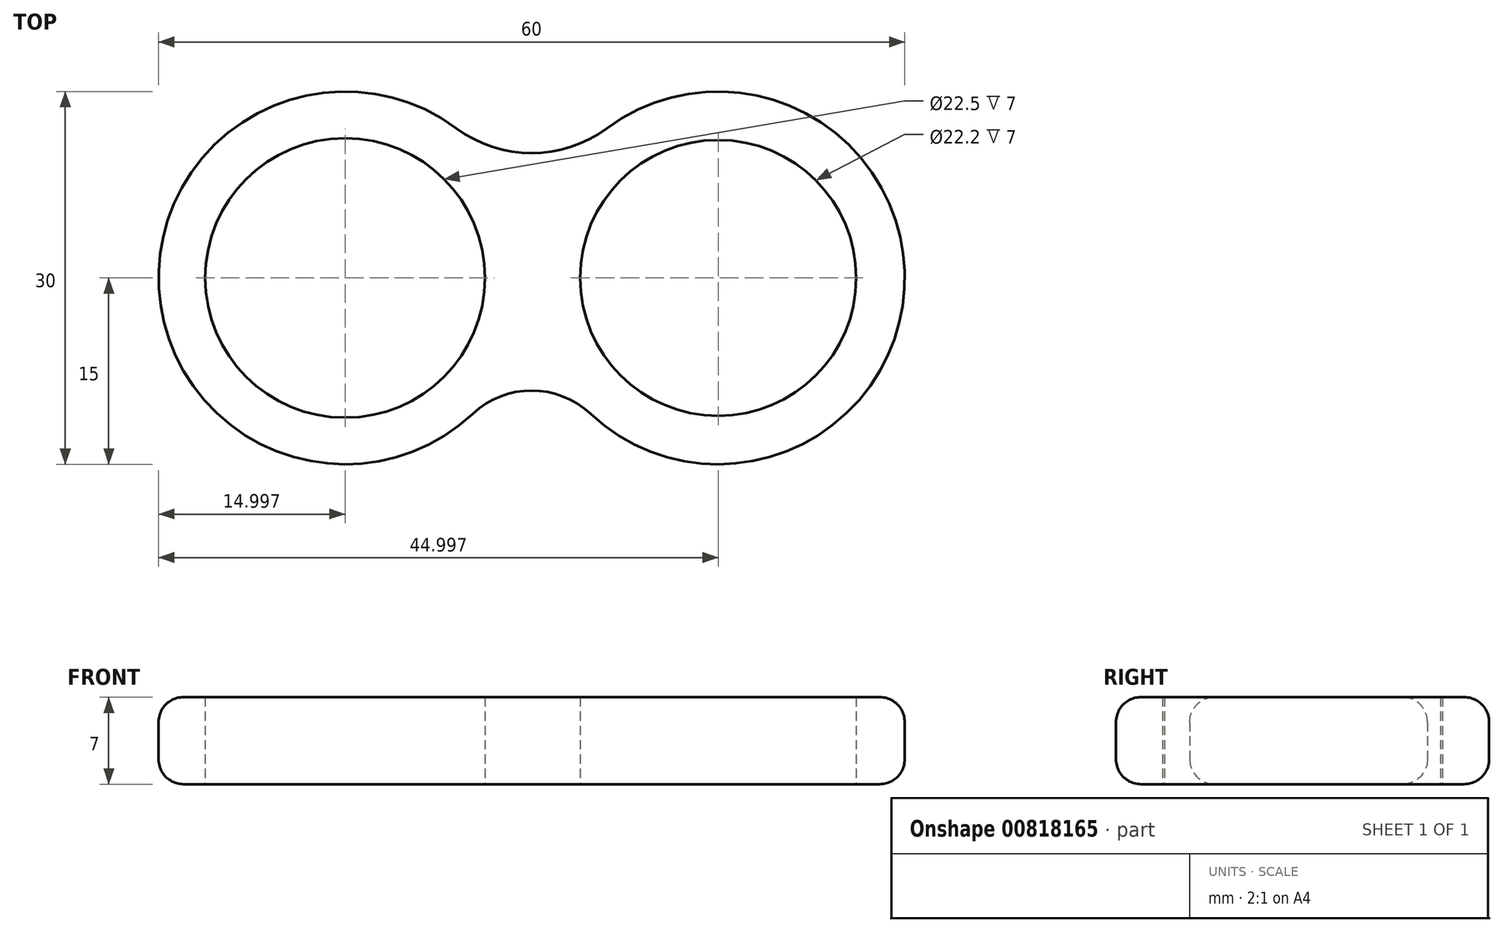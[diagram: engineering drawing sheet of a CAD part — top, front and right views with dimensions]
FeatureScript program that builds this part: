
annotation { "Feature Type Name" : "Feature", "Feature Type Description" : "" }
export const myFeature = defineFeature(function(context is Context, id is Id, definition is map)
    precondition{}
    {
        {
            var Q0;
            Q0=qCreatedBy(makeId("Top.planeOp"),FACE);
            var sketch = newSketch(context, id + "F0", { "sketchPlane" : qUnion([Q0])});
            skCircle(sketch, "E0", {"center": v(-16.77, 0) * mm, "radius": 11.25 * mm});
            skCircle(sketch, "E1", {"center": v(13.23, 0) * mm, "radius": 11.1 * mm});
            skArc(sketch, "E2", {"start": v(-7.83, 12.04) * mm, "mid": v(-31.75, -0.86) * mm, "end": v(-6.52, -10.94) * mm});
            skArc(sketch, "E3", {"start": v(2.97, -10.94) * mm, "mid": v(28.2, -0.86) * mm, "end": v(4.28, 12.04) * mm});
            skArc(sketch, "E4", {"start": v(-7.83, 12.04) * mm, "mid": v(-1.77, 10.04) * mm, "end": v(4.28, 12.04) * mm});
            skArc(sketch, "E5", {"start": v(2.97, -10.94) * mm, "mid": v(-1.77, -9.07) * mm, "end": v(-6.52, -10.94) * mm});
            skSolve(sketch);
        }
        {
            var Q0;
            Q0 = qSketchRegion(id + "F0", true);
            extrude(context, id + "F1", {"entities" : qUnion([Q0]), "depth" : 7 * mm, "offsetDistance" : 25 * mm});
        }
        {
            var Q0;
            Q0=makeQuery(id+"F1.opExtrude","CAP_EDGE",EDGE,{"disambiguationData":[OSD([sQuery(id+"F0.wireOp",EDGE,"E2")])],"isStart":true});
            var Q1;
            Q1=makeQuery(id+"F1.opExtrude","CAP_EDGE",EDGE,{"disambiguationData":[OSD([sQuery(id+"F0.wireOp",EDGE,"E3")])],"isStart":false});
            fillet(context, id + "F2", {"entities" : qUnion([Q0, Q1]), "radius" : 2 * mm, "tangentPropagation" : true, "allowEdgeOverflow" : false});
        }
    });
